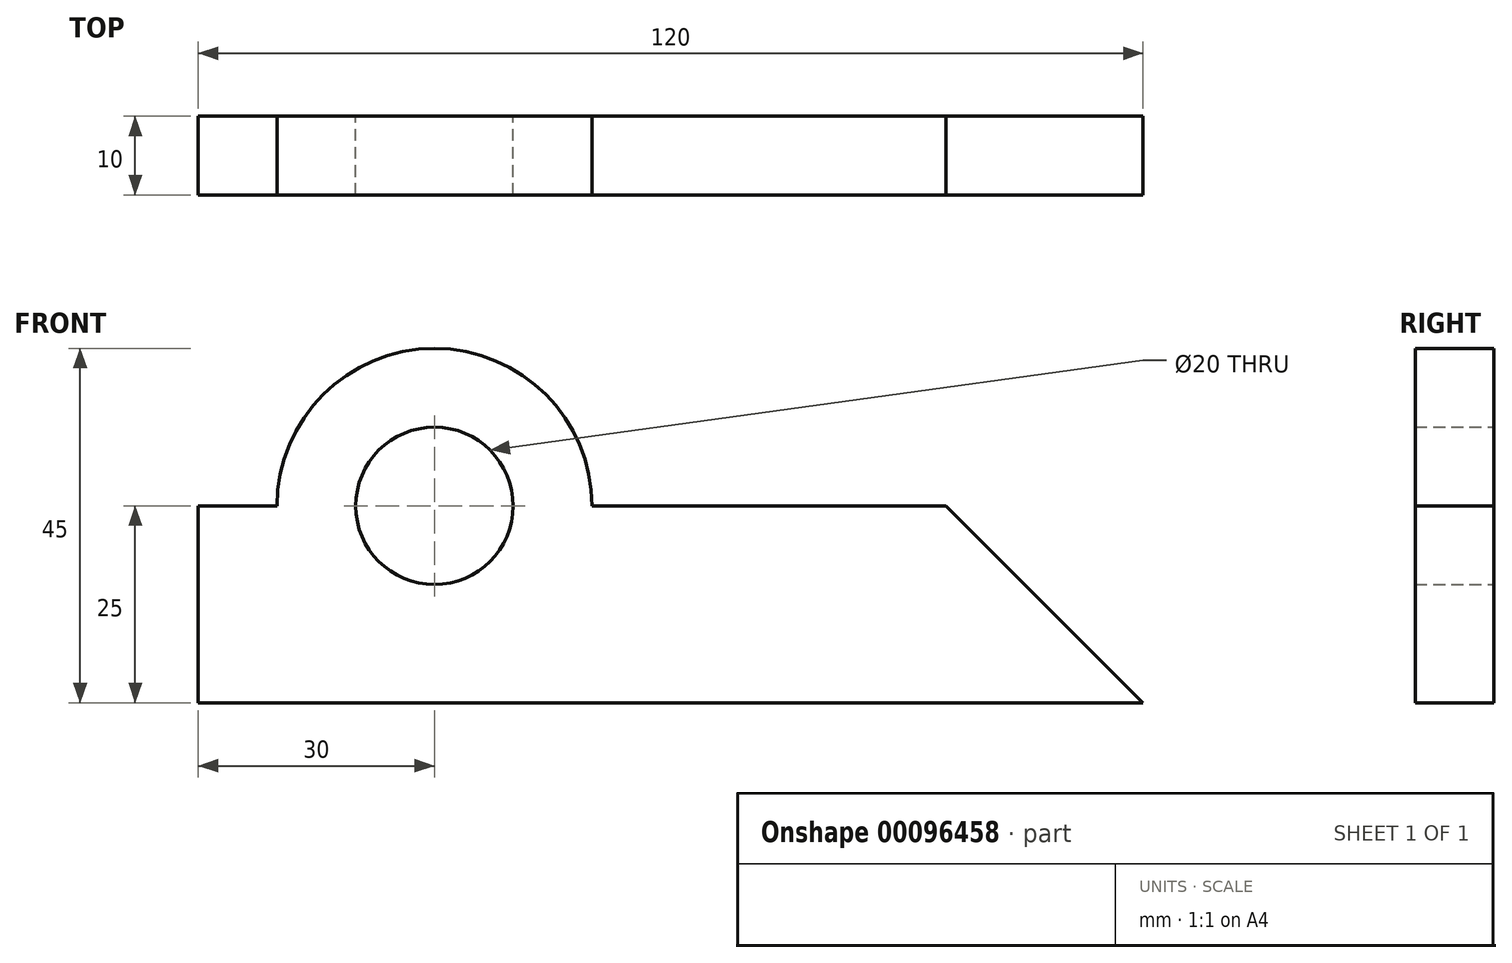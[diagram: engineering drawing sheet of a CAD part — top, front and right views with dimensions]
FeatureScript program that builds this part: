
annotation { "Feature Type Name" : "Feature", "Feature Type Description" : "" }
export const myFeature = defineFeature(function(context is Context, id is Id, definition is map)
    precondition{}
    {
        {
            var Q0;
            Q0=qCreatedBy(makeId("Front.planeOp"),FACE);
            var sketch = newSketch(context, id + "F0", { "sketchPlane" : qUnion([Q0])});
            skLineSegment(sketch, "E0", {"start": v(0, 0) * mm, "end": v(120, 0) * mm});
            skLineSegment(sketch, "E1", {"start": v(120, 0) * mm, "end": v(95, 25) * mm});
            skLineSegment(sketch, "E2", {"start": v(95, 25) * mm, "end": v(50, 25) * mm});
            skLineSegment(sketch, "E3", {"start": v(0, 0) * mm, "end": v(0, 25) * mm});
            skLineSegment(sketch, "E4", {"start": v(0, 25) * mm, "end": v(10, 25) * mm});
            skLineSegment(sketch, "E5", {"start": v(10, 25) * mm, "end": v(50, 25) * mm, "construction": true});
            skArc(sketch, "E6", {"start": v(10, 25) * mm, "mid": v(30, 45) * mm, "end": v(50, 25) * mm});
            skCircle(sketch, "E7", {"center": v(30, 25) * mm, "radius": 10 * mm});
            skSolve(sketch);
        }
        {
            var Q0;
            Q0 = qSketchRegion(id + "F0", true);
            extrude(context, id + "F1", {"entities" : qUnion([Q0]), "depth" : 10 * mm});
        }
    });
